# Revit family: Aballs_A_ll_ME_Wall
name_source: partatom
category: Luminarias
revit_build: Autodesk Revit 2017 (Build: 20160225_1515(x64)
units: mm (PartAtom-declared; Revit-internal decimal feet)

## family parameters
Anfitrión = Muro
Compartido = No
Corte con vacíos al cargar = No
Cota de conector redondo = Diámetro de uso
Número OmniClass = 23.80.70.00
Origen de luz = Sí
Punto de cálculo de habitación = No
Siempre vertical = Sí
Tipo de pieza = Normal
Título OmniClass = Lighting

## types (1)
- Aballs_A_ll_ME_Wall
    Base = Shiny  Golden
    Cambio de temperatura de color de luz atenuada = <Ninguno>
    Descripción = Ceiling lamp. Base in white, black, golden, copper or platinum ceramic. Diffuser in blown opal matt glass.
    Difusor = Opal White
    Fabricante = PARACHILNA
    Filtro de color = 16777215
    Imagen de tipo = w3AFNegw.jpeg
    Metal Ring = Shiny  Platinum
    Modelo = ABALLS A II ME
    Montaje = https://www.dropbox.com
    Tamaño de símbolo de origen de luz = 610 mm
    URL = https://www.parachilna.eu
